# Revit family: ASSA_ABLOY_DockLeveler_DL6010S
name_source: partatom
category: Specialty Equipment
units: mm (PartAtom-declared; Revit-internal decimal feet)

## family parameters
Always vertical = Yes
Cut with Voids When Loaded = No
Host = Floor
Part Type = Normal
Room Calculation Point = No
Round Connector Dimension = Use Diameter
Shared = No

## types (2) — shared parameters
DL6010S_BentLip = DL6010S_LevelerTop : DL6010S_BentLip
DL6010S_StraightLip = DL6010S_LevelerTop : DL6010S_StraightLip
Description = Docking Leveler
Manufacturer = ASSA ABLOY
Model = DL6010S
TailLiftWidth = 3000 mm  [stored 9.84252 ft]

## per-type parameters (varying)
| type | LipType | URL |
| Bent Lip | DL6010S_LevelerTop : DL6010S_BentLip |  |
| Straight Lip | DL6010S_LevelerTop : DL6010S_StraightLip | https://www.assaabloyentrance.com |

note: [stored X ft] marks values corroborated as IEEE doubles in the binary element streams (Revit-internal decimal feet)

## geometry (parser evidence)
native form markers: Sweep x10
no freeform markers — native parametric forms only
